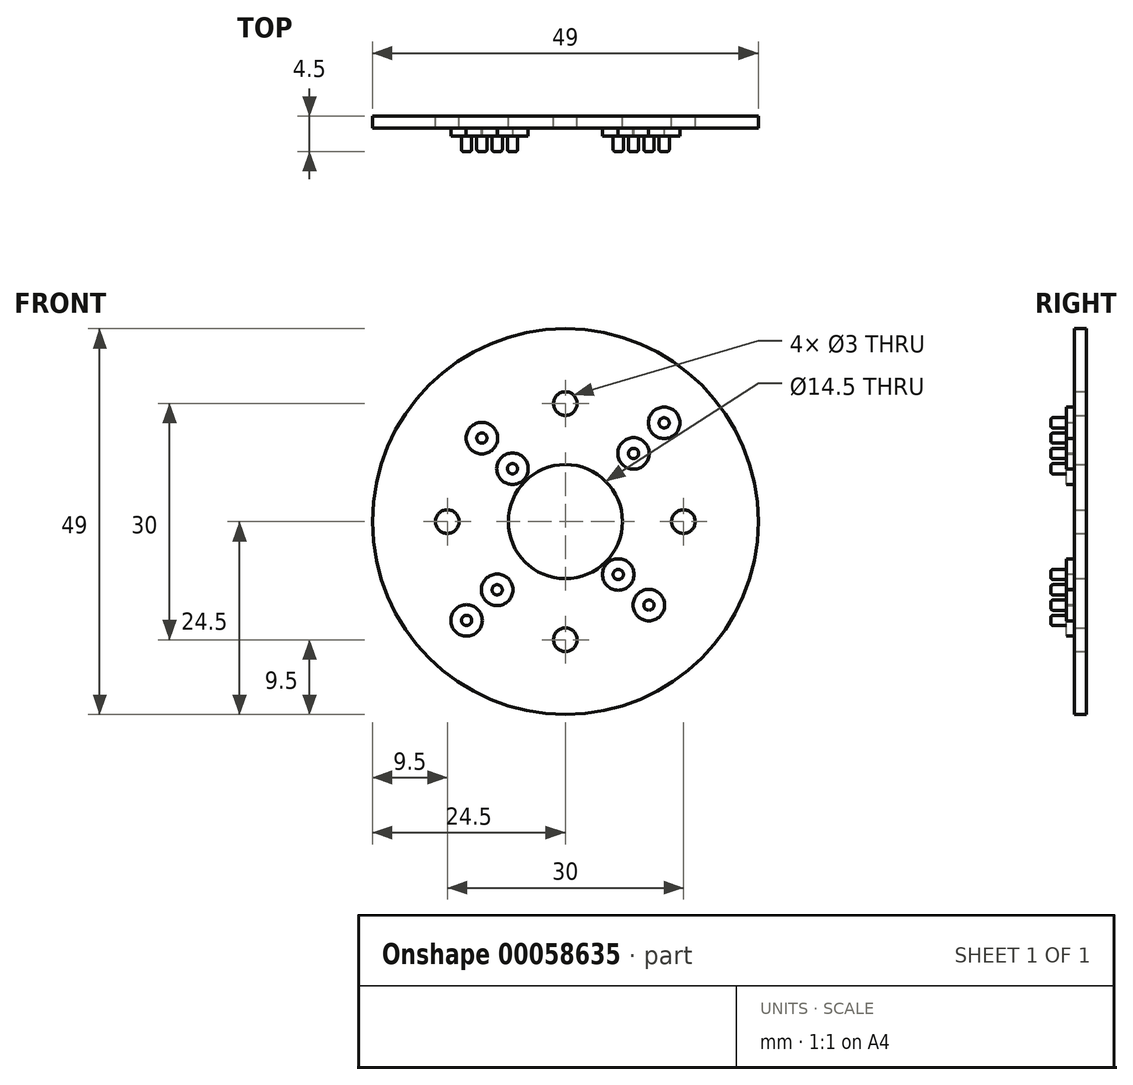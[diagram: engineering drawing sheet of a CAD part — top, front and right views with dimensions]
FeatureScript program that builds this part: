
annotation { "Feature Type Name" : "Feature", "Feature Type Description" : "" }
export const myFeature = defineFeature(function(context is Context, id is Id, definition is map)
    precondition{}
    {
        {
            var Q0;
            Q0=qCreatedBy(makeId("Front.planeOp"),FACE);
            var sketch = newSketch(context, id + "F0", { "sketchPlane" : qUnion([Q0])});
            skCircle(sketch, "E0", {"center": v(0, 0) * mm, "radius": 24.5 * mm});
            skCircle(sketch, "E1", {"center": v(0, 0) * mm, "radius": 7.25 * mm});
            skCircle(sketch, "E2", {"center": v(0, -15) * mm, "radius": 1.5 * mm});
            skCircle(sketch, "E3", {"center": v(15, 0) * mm, "radius": 1.5 * mm});
            skCircle(sketch, "E4", {"center": v(0, 15) * mm, "radius": 1.5 * mm});
            skCircle(sketch, "E5", {"center": v(-15, 0) * mm, "radius": 1.5 * mm});
            skLineSegment(sketch, "E6", {"start": v(-31.24, 0) * mm, "end": v(0, 0) * mm, "construction": true});
            skLineSegment(sketch, "E7", {"start": v(0, 0) * mm, "end": v(0, -25.93) * mm, "construction": true});
            skLineSegment(sketch, "E8", {"start": v(0, 0) * mm, "end": v(26.9, 0) * mm, "construction": true});
            skLineSegment(sketch, "E9", {"start": v(0, 0) * mm, "end": v(0, 20.37) * mm, "construction": true});
            skCircle(sketch, "E10", {"center": v(0, 0) * mm, "radius": 15 * mm, "construction": true});
            skSolve(sketch);
        }
        {
            var Q0;
            Q0=makeQuery(id+"F0.imprint","IMPRINT",FACE,{"disambiguationData":[TD([[makeQuery(id+"F0.imprint","IMPRINT",EDGE,{"derivedFrom":sQuery(id+"F0.wireOp",EDGE,"E0")}),1.0]])]});
            var Q1;
            Q1=makeQuery(id+"F0.imprint","IMPRINT",FACE,{"disambiguationData":[TD([[makeQuery(id+"F0.imprint","IMPRINT",EDGE,{"derivedFrom":sQuery(id+"F0.wireOp",EDGE,"E5")}),-1.0]])]});
            var Q2;
            Q2=makeQuery(id+"F0.imprint","IMPRINT",FACE,{"disambiguationData":[TD([[makeQuery(id+"F0.imprint","IMPRINT",EDGE,{"derivedFrom":sQuery(id+"F0.wireOp",EDGE,"E4")}),-1.0]])]});
            var Q3;
            Q3=makeQuery(id+"F0.imprint","IMPRINT",FACE,{"disambiguationData":[TD([[makeQuery(id+"F0.imprint","IMPRINT",EDGE,{"derivedFrom":sQuery(id+"F0.wireOp",EDGE,"E2")}),-1.0]])]});
            var Q4;
            Q4=makeQuery(id+"F0.imprint","IMPRINT",FACE,{"disambiguationData":[TD([[makeQuery(id+"F0.imprint","IMPRINT",EDGE,{"derivedFrom":sQuery(id+"F0.wireOp",EDGE,"E3")}),-1.0]])]});
            extrude(context, id + "F1", {"entities" : qUnion([Q0, Q1, Q2, Q3, Q4]), "depth" : 1.5 * mm});
        }
        {
            var Q0;
            Q0=makeQuery(id+"F1.opExtrude","CAP_FACE",FACE,{"disambiguationData":[OSD([sQuery(id+"F0.wireOp",EDGE,"E0"),sQuery(id+"F0.wireOp",EDGE,"E1"),sQuery(id+"F0.wireOp",EDGE,"E2"),sQuery(id+"F0.wireOp",EDGE,"E3"),sQuery(id+"F0.wireOp",EDGE,"E4"),sQuery(id+"F0.wireOp",EDGE,"E5")])],"isStart":false});
            var sketch = newSketch(context, id + "F2", { "sketchPlane" : qUnion([Q0])});
            skCircle(sketch, "E11", {"center": v(-12.55, -12.55) * mm, "radius": 2 * mm});
            skCircle(sketch, "E12", {"center": v(-12.55, -12.55) * mm, "radius": 0.65 * mm});
            skCircle(sketch, "E13", {"center": v(0, 0) * mm, "radius": 12.25 * mm, "construction": true});
            skCircle(sketch, "E14", {"center": v(0, 0) * mm, "radius": 9.5 * mm, "construction": true});
            skCircle(sketch, "E15", {"center": v(0, 0) * mm, "radius": 15 * mm, "construction": true});
            skCircle(sketch, "E16", {"center": v(0, 0) * mm, "radius": 17.75 * mm, "construction": true});
            skLineSegment(sketch, "E17", {"start": v(0, 0) * mm, "end": v(-20.68, 20.68) * mm, "construction": true});
            skLineSegment(sketch, "E18", {"start": v(0, 0) * mm, "end": v(19.64, 19.64) * mm, "construction": true});
            skLineSegment(sketch, "E19", {"start": v(0, 0) * mm, "end": v(19.28, -19.28) * mm, "construction": true});
            skLineSegment(sketch, "E20", {"start": v(0, 0) * mm, "end": v(-19.48, -19.48) * mm, "construction": true});
            skCircle(sketch, "E21", {"center": v(-8.66, -8.66) * mm, "radius": 2 * mm});
            skCircle(sketch, "E22", {"center": v(-8.66, -8.66) * mm, "radius": 0.65 * mm});
            skCircle(sketch, "E23", {"center": v(8.66, 8.66) * mm, "radius": 2 * mm});
            skCircle(sketch, "E24", {"center": v(8.66, 8.66) * mm, "radius": 0.65 * mm});
            skCircle(sketch, "E25", {"center": v(12.55, 12.55) * mm, "radius": 2 * mm});
            skCircle(sketch, "E26", {"center": v(12.55, 12.55) * mm, "radius": 0.65 * mm});
            skCircle(sketch, "E27", {"center": v(6.72, -6.72) * mm, "radius": 2 * mm});
            skCircle(sketch, "E28", {"center": v(6.72, -6.72) * mm, "radius": 0.65 * mm});
            skCircle(sketch, "E29", {"center": v(10.6, -10.6) * mm, "radius": 2 * mm});
            skCircle(sketch, "E30", {"center": v(10.6, -10.6) * mm, "radius": 0.65 * mm});
            skCircle(sketch, "E31", {"center": v(-6.72, 6.72) * mm, "radius": 2 * mm});
            skCircle(sketch, "E32", {"center": v(-6.72, 6.72) * mm, "radius": 0.65 * mm});
            skCircle(sketch, "E33", {"center": v(-10.6, 10.6) * mm, "radius": 2 * mm});
            skCircle(sketch, "E34", {"center": v(-10.6, 10.6) * mm, "radius": 0.65 * mm});
            skSolve(sketch);
        }
        {
            var Q0;
            Q0=makeQuery(id+"F2.imprint","IMPRINT",FACE,{"disambiguationData":[TD([[makeQuery(id+"F2.imprint","IMPRINT",EDGE,{"derivedFrom":sQuery(id+"F2.wireOp",EDGE,"E11")}),1.0]])]});
            var Q1;
            Q1=makeQuery(id+"F2.imprint","IMPRINT",FACE,{"disambiguationData":[TD([[makeQuery(id+"F2.imprint","IMPRINT",EDGE,{"derivedFrom":sQuery(id+"F2.wireOp",EDGE,"E21")}),1.0]])]});
            var Q2;
            Q2=makeQuery(id+"F2.imprint","IMPRINT",FACE,{"disambiguationData":[TD([[makeQuery(id+"F2.imprint","IMPRINT",EDGE,{"derivedFrom":sQuery(id+"F2.wireOp",EDGE,"E33")}),1.0]])]});
            var Q3;
            Q3=makeQuery(id+"F2.imprint","IMPRINT",FACE,{"disambiguationData":[TD([[makeQuery(id+"F2.imprint","IMPRINT",EDGE,{"derivedFrom":sQuery(id+"F2.wireOp",EDGE,"E31")}),1.0]])]});
            var Q4;
            Q4=makeQuery(id+"F2.imprint","IMPRINT",FACE,{"disambiguationData":[TD([[makeQuery(id+"F2.imprint","IMPRINT",EDGE,{"derivedFrom":sQuery(id+"F2.wireOp",EDGE,"E23")}),1.0]])]});
            var Q5;
            Q5=makeQuery(id+"F2.imprint","IMPRINT",FACE,{"disambiguationData":[TD([[makeQuery(id+"F2.imprint","IMPRINT",EDGE,{"derivedFrom":sQuery(id+"F2.wireOp",EDGE,"E25")}),1.0]])]});
            var Q6;
            Q6=makeQuery(id+"F2.imprint","IMPRINT",FACE,{"disambiguationData":[TD([[makeQuery(id+"F2.imprint","IMPRINT",EDGE,{"derivedFrom":sQuery(id+"F2.wireOp",EDGE,"E27")}),1.0]])]});
            var Q7;
            Q7=makeQuery(id+"F2.imprint","IMPRINT",FACE,{"disambiguationData":[TD([[makeQuery(id+"F2.imprint","IMPRINT",EDGE,{"derivedFrom":sQuery(id+"F2.wireOp",EDGE,"E29")}),1.0]])]});
            extrude(context, id + "F3", {"entities" : qUnion([Q0, Q1, Q2, Q3, Q4, Q5, Q6, Q7]), "operationType" : NewBodyOperationType.ADD, "depth" : 1 * mm});
        }
        {
            var Q0;
            Q0=makeQuery(id+"F2.imprint","IMPRINT",FACE,{"disambiguationData":[TD([[makeQuery(id+"F2.imprint","IMPRINT",EDGE,{"derivedFrom":sQuery(id+"F2.wireOp",EDGE,"E22")}),1.0]])]});
            var Q1;
            Q1=makeQuery(id+"F2.imprint","IMPRINT",FACE,{"disambiguationData":[TD([[makeQuery(id+"F2.imprint","IMPRINT",EDGE,{"derivedFrom":sQuery(id+"F2.wireOp",EDGE,"E28")}),1.0]])]});
            var Q2;
            Q2=makeQuery(id+"F2.imprint","IMPRINT",FACE,{"disambiguationData":[TD([[makeQuery(id+"F2.imprint","IMPRINT",EDGE,{"derivedFrom":sQuery(id+"F2.wireOp",EDGE,"E30")}),1.0]])]});
            var Q3;
            Q3=makeQuery(id+"F2.imprint","IMPRINT",FACE,{"disambiguationData":[TD([[makeQuery(id+"F2.imprint","IMPRINT",EDGE,{"derivedFrom":sQuery(id+"F2.wireOp",EDGE,"E24")}),1.0]])]});
            var Q4;
            Q4=makeQuery(id+"F2.imprint","IMPRINT",FACE,{"disambiguationData":[TD([[makeQuery(id+"F2.imprint","IMPRINT",EDGE,{"derivedFrom":sQuery(id+"F2.wireOp",EDGE,"E26")}),1.0]])]});
            var Q5;
            Q5=makeQuery(id+"F2.imprint","IMPRINT",FACE,{"disambiguationData":[TD([[makeQuery(id+"F2.imprint","IMPRINT",EDGE,{"derivedFrom":sQuery(id+"F2.wireOp",EDGE,"E32")}),1.0]])]});
            var Q6;
            Q6=makeQuery(id+"F2.imprint","IMPRINT",FACE,{"disambiguationData":[TD([[makeQuery(id+"F2.imprint","IMPRINT",EDGE,{"derivedFrom":sQuery(id+"F2.wireOp",EDGE,"E34")}),1.0]])]});
            var Q7;
            Q7=makeQuery(id+"F2.imprint","IMPRINT",FACE,{"disambiguationData":[TD([[makeQuery(id+"F2.imprint","IMPRINT",EDGE,{"derivedFrom":sQuery(id+"F2.wireOp",EDGE,"E12")}),1.0]])]});
            extrude(context, id + "F4", {"entities" : qUnion([Q0, Q1, Q2, Q3, Q4, Q5, Q6, Q7]), "operationType" : NewBodyOperationType.ADD, "depth" : 3 * mm});
        }
        {
            var Q0;
            Q0=makeQuery(id+"F4.opExtrude","CAP_EDGE",EDGE,{"disambiguationData":[OSD([sQuery(id+"F2.wireOp",EDGE,"E12")])],"isStart":false});
            var Q1;
            Q1=makeQuery(id+"F4.opExtrude","CAP_EDGE",EDGE,{"disambiguationData":[OSD([sQuery(id+"F2.wireOp",EDGE,"E22")])],"isStart":false});
            var Q2;
            Q2=makeQuery(id+"F4.opExtrude","CAP_EDGE",EDGE,{"disambiguationData":[OSD([sQuery(id+"F2.wireOp",EDGE,"E28")])],"isStart":false});
            var Q3;
            Q3=makeQuery(id+"F4.opExtrude","CAP_EDGE",EDGE,{"disambiguationData":[OSD([sQuery(id+"F2.wireOp",EDGE,"E30")])],"isStart":false});
            var Q4;
            Q4=makeQuery(id+"F4.opExtrude","CAP_EDGE",EDGE,{"disambiguationData":[OSD([sQuery(id+"F2.wireOp",EDGE,"E32")])],"isStart":false});
            var Q5;
            Q5=makeQuery(id+"F4.opExtrude","CAP_EDGE",EDGE,{"disambiguationData":[OSD([sQuery(id+"F2.wireOp",EDGE,"E34")])],"isStart":false});
            var Q6;
            Q6=makeQuery(id+"F4.opExtrude","CAP_EDGE",EDGE,{"disambiguationData":[OSD([sQuery(id+"F2.wireOp",EDGE,"E24")])],"isStart":false});
            var Q7;
            Q7=makeQuery(id+"F4.opExtrude","CAP_EDGE",EDGE,{"disambiguationData":[OSD([sQuery(id+"F2.wireOp",EDGE,"E26")])],"isStart":false});
            fillet(context, id + "F5", {"entities" : qUnion([Q0, Q1, Q2, Q3, Q4, Q5, Q6, Q7]), "radius" : 0.3 * mm, "tangentPropagation" : true, "allowEdgeOverflow" : false});
        }
    });
